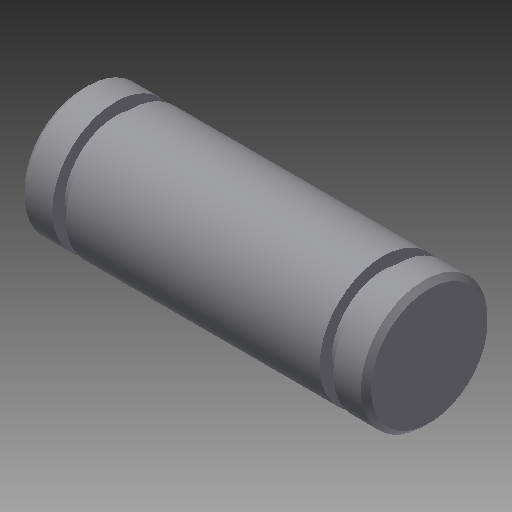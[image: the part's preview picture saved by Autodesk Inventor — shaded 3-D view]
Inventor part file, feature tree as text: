
AUTODESK INVENTOR PART (.ipt)
format: ipt  version: 2019.4 (Build 234330000, 330)  size: 151,040 bytes
history: native  units: in
note: dims shown in document units (in); Inventor stores cm internally (conversion verified against a paired STEP export)
features: other x49, revolve x1, sketch x1
ambient origin geometry x8: Origin, YZ Plane, XZ Plane, XY Plane, X Axis, Y Axis, Z Axis, Center Point
bodies: Solid1 (feature_tree)
feature tree (51):
  revolve  "Revolution1"  [1 undecoded]
  other  "p1_XY"
  other  "p1_YZ"
  other  "p1_ZX"
  other  "p1_X"
  other  "p1_Y"
  other  "p1_Z"
  other  "p1_Center"
  other  "p2_XY"
  other  "p2_YZ"
  other  "p2_ZX"
  other  "p2_X"
  other  "p2_Y"
  other  "p2_Z"
  other  "p2_Center"
  other  "pin_XY"
  other  "pin_YZ"
  other  "pin_ZX"
  other  "pin_X"
  other  "pin_Y"
  other  "pin_Z"
  other  "pin_Center"
  other  "rr1_XY"
  other  "rr1_YZ"
  other  "rr1_ZX"
  other  "rr1_X"
  other  "rr1_Y"
  other  "rr1_Z"
  other  "rr1_Center"
  other  "rr2_XY"
  other  "rr2_YZ"
  other  "rr2_ZX"
  other  "rr2_X"
  other  "rr2_Y"
  other  "rr2_Z"
  other  "rr2_Center"
  other  "w21_XY"
  other  "w21_YZ"
  other  "w21_ZX"
  other  "w21_X"
  other  "w21_Y"
  other  "w21_Z"
  other  "w21_Center"
  other  "w22_XY"
  other  "w22_YZ"
  other  "w22_ZX"
  other  "w22_X"
  other  "w22_Y"
  other  "w22_Z"
  other  "w22_Center"
  sketch  "Sketch_1"  dims[d0=360.0deg]
note: 1 required parameter value undecoded (feature->parameter linkage not recoverable at this tier; creation-order binding heuristic only, values carry confidence <= 0.55)
